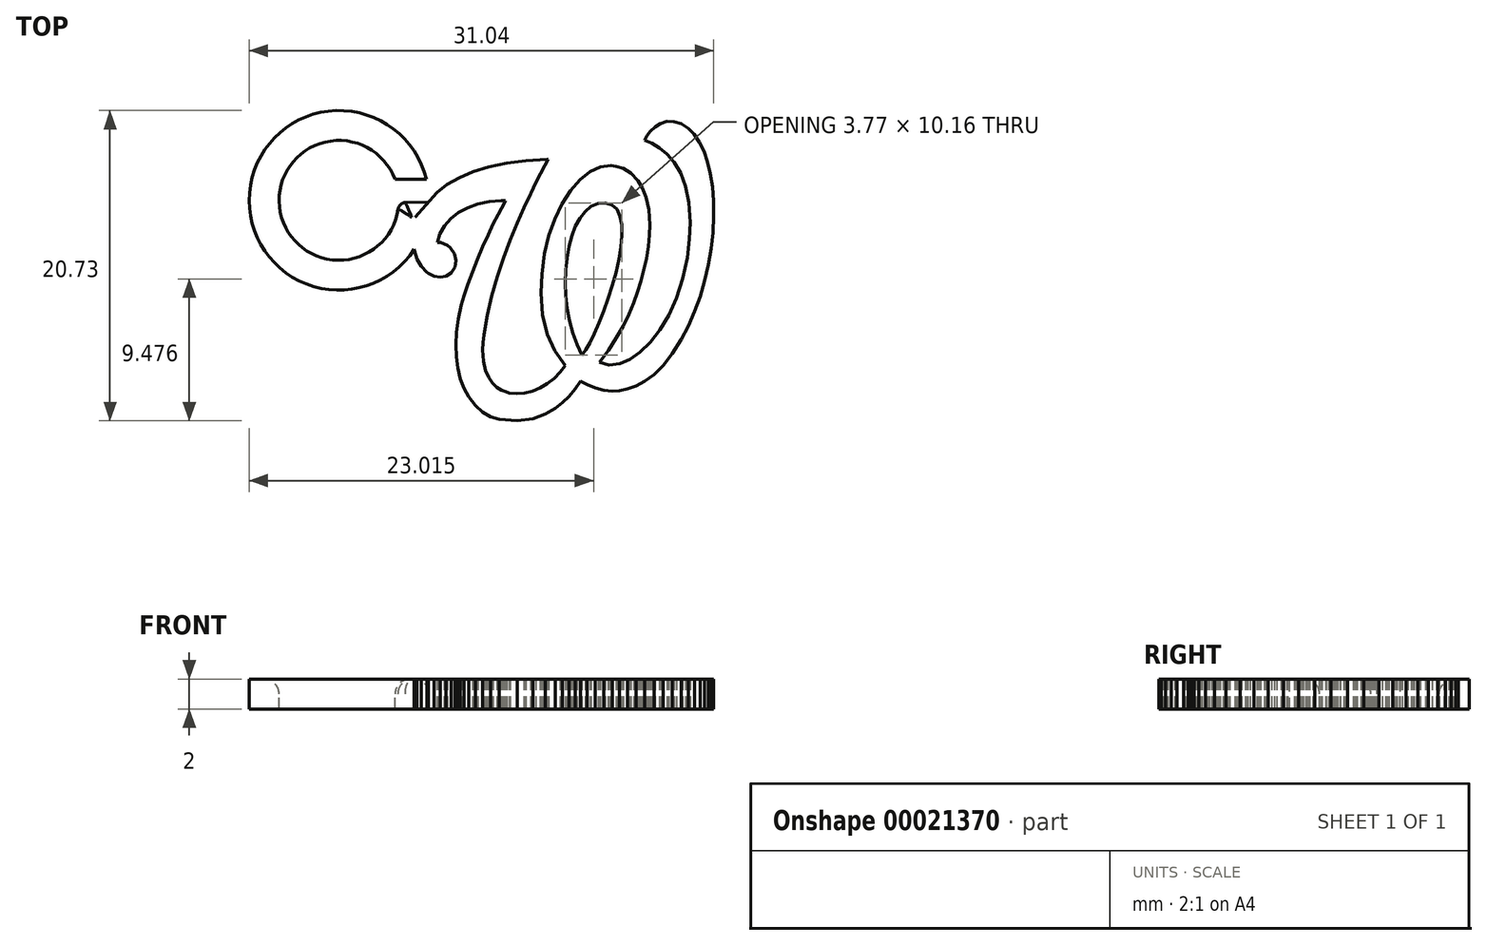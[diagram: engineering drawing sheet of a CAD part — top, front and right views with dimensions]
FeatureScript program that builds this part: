
annotation { "Feature Type Name" : "Feature", "Feature Type Description" : "" }
export const myFeature = defineFeature(function(context is Context, id is Id, definition is map)
    precondition{}
    {
        {
            var Q0;
            Q0=qCreatedBy(makeId("Top.planeOp"),FACE);
            var sketch = newSketch(context, id + "F0", { "sketchPlane" : qUnion([Q0])});
            skLineSegment(sketch, "E0", {"start": v(8.32, 9.54) * mm, "end": v(7.85, 9.84) * mm});
            skLineSegment(sketch, "E1", {"start": v(7.85, 9.84) * mm, "end": v(7.38, 10) * mm});
            skLineSegment(sketch, "E2", {"start": v(7.38, 10) * mm, "end": v(6.9, 10) * mm});
            skLineSegment(sketch, "E3", {"start": v(6.9, 10) * mm, "end": v(6.45, 9.86) * mm});
            skLineSegment(sketch, "E4", {"start": v(6.45, 9.86) * mm, "end": v(6.1, 9.64) * mm});
            skLineSegment(sketch, "E5", {"start": v(6.1, 9.64) * mm, "end": v(5.8, 9.36) * mm});
            skLineSegment(sketch, "E6", {"start": v(5.8, 9.36) * mm, "end": v(5.58, 9.04) * mm});
            skLineSegment(sketch, "E7", {"start": v(5.58, 9.04) * mm, "end": v(5.43, 8.73) * mm});
            skLineSegment(sketch, "E8", {"start": v(5.43, 8.73) * mm, "end": v(5.9, 8.53) * mm});
            skLineSegment(sketch, "E9", {"start": v(5.9, 8.53) * mm, "end": v(6.4, 8.24) * mm});
            skLineSegment(sketch, "E10", {"start": v(6.4, 8.24) * mm, "end": v(6.92, 7.83) * mm});
            skLineSegment(sketch, "E11", {"start": v(6.92, 7.83) * mm, "end": v(7.4, 7.27) * mm});
            skLineSegment(sketch, "E12", {"start": v(7.4, 7.27) * mm, "end": v(7.82, 6.56) * mm});
            skLineSegment(sketch, "E13", {"start": v(7.82, 6.56) * mm, "end": v(8.15, 5.66) * mm});
            skLineSegment(sketch, "E14", {"start": v(8.15, 5.66) * mm, "end": v(8.38, 4.56) * mm});
            skLineSegment(sketch, "E15", {"start": v(8.38, 4.56) * mm, "end": v(8.46, 3.25) * mm});
            skLineSegment(sketch, "E16", {"start": v(8.46, 3.25) * mm, "end": v(8.41, 2.13) * mm});
            skLineSegment(sketch, "E17", {"start": v(8.41, 2.13) * mm, "end": v(8.26, 0.9) * mm});
            skLineSegment(sketch, "E18", {"start": v(8.26, 0.9) * mm, "end": v(7.97, -0.51) * mm});
            skLineSegment(sketch, "E19", {"start": v(7.97, -0.51) * mm, "end": v(7.55, -1.8) * mm});
            skLineSegment(sketch, "E20", {"start": v(7.55, -1.8) * mm, "end": v(7.03, -2.93) * mm});
            skLineSegment(sketch, "E21", {"start": v(7.03, -2.93) * mm, "end": v(6.43, -3.92) * mm});
            skLineSegment(sketch, "E22", {"start": v(6.43, -3.92) * mm, "end": v(5.78, -4.75) * mm});
            skLineSegment(sketch, "E23", {"start": v(5.78, -4.75) * mm, "end": v(5.1, -5.41) * mm});
            skLineSegment(sketch, "E24", {"start": v(5.1, -5.41) * mm, "end": v(4.42, -5.9) * mm});
            skLineSegment(sketch, "E25", {"start": v(4.42, -5.9) * mm, "end": v(3.75, -6.18) * mm});
            skLineSegment(sketch, "E26", {"start": v(3.75, -6.18) * mm, "end": v(3.02, -6.27) * mm});
            skLineSegment(sketch, "E27", {"start": v(3.02, -6.27) * mm, "end": v(2.39, -6.08) * mm});
            skLineSegment(sketch, "E28", {"start": v(2.39, -6.08) * mm, "end": v(3, -5.28) * mm});
            skLineSegment(sketch, "E29", {"start": v(3, -5.28) * mm, "end": v(3.52, -4.47) * mm});
            skLineSegment(sketch, "E30", {"start": v(3.52, -4.47) * mm, "end": v(3.97, -3.67) * mm});
            skLineSegment(sketch, "E31", {"start": v(3.97, -3.67) * mm, "end": v(4.36, -2.88) * mm});
            skLineSegment(sketch, "E32", {"start": v(4.36, -2.88) * mm, "end": v(4.68, -2.12) * mm});
            skLineSegment(sketch, "E33", {"start": v(4.68, -2.12) * mm, "end": v(4.95, -1.39) * mm});
            skLineSegment(sketch, "E34", {"start": v(4.95, -1.39) * mm, "end": v(5.16, -0.7) * mm});
            skLineSegment(sketch, "E35", {"start": v(5.16, -0.7) * mm, "end": v(5.33, -0.06) * mm});
            skLineSegment(sketch, "E36", {"start": v(5.33, -0.06) * mm, "end": v(5.53, 0.84) * mm});
            skLineSegment(sketch, "E37", {"start": v(5.53, 0.84) * mm, "end": v(5.66, 1.67) * mm});
            skLineSegment(sketch, "E38", {"start": v(5.66, 1.67) * mm, "end": v(5.74, 2.4) * mm});
            skLineSegment(sketch, "E39", {"start": v(5.74, 2.4) * mm, "end": v(5.76, 3.08) * mm});
            skLineSegment(sketch, "E40", {"start": v(5.76, 3.08) * mm, "end": v(5.7, 4.1) * mm});
            skLineSegment(sketch, "E41", {"start": v(5.7, 4.1) * mm, "end": v(5.52, 4.93) * mm});
            skLineSegment(sketch, "E42", {"start": v(5.52, 4.93) * mm, "end": v(5.26, 5.57) * mm});
            skLineSegment(sketch, "E43", {"start": v(5.26, 5.57) * mm, "end": v(4.97, 6.05) * mm});
            skLineSegment(sketch, "E44", {"start": v(4.97, 6.05) * mm, "end": v(4.48, 6.56) * mm});
            skLineSegment(sketch, "E45", {"start": v(4.48, 6.56) * mm, "end": v(3.98, 6.86) * mm});
            skLineSegment(sketch, "E46", {"start": v(3.98, 6.86) * mm, "end": v(3.52, 7) * mm});
            skLineSegment(sketch, "E47", {"start": v(3.52, 7) * mm, "end": v(3.15, 7.06) * mm});
            skLineSegment(sketch, "E48", {"start": v(3.15, 7.06) * mm, "end": v(2.46, 6.96) * mm});
            skLineSegment(sketch, "E49", {"start": v(2.46, 6.96) * mm, "end": v(1.77, 6.64) * mm});
            skLineSegment(sketch, "E50", {"start": v(1.77, 6.64) * mm, "end": v(1.1, 6.1) * mm});
            skLineSegment(sketch, "E51", {"start": v(1.1, 6.1) * mm, "end": v(0.47, 5.37) * mm});
            skLineSegment(sketch, "E52", {"start": v(0.47, 5.37) * mm, "end": v(-0.1, 4.5) * mm});
            skLineSegment(sketch, "E53", {"start": v(-0.1, 4.5) * mm, "end": v(-0.6, 3.48) * mm});
            skLineSegment(sketch, "E54", {"start": v(-0.6, 3.48) * mm, "end": v(-1, 2.36) * mm});
            skLineSegment(sketch, "E55", {"start": v(-1, 2.36) * mm, "end": v(-1.27, 1.16) * mm});
            skLineSegment(sketch, "E56", {"start": v(-1.27, 1.16) * mm, "end": v(-1.46, -0.2) * mm});
            skLineSegment(sketch, "E57", {"start": v(-1.46, -0.2) * mm, "end": v(-1.52, -1.46) * mm});
            skLineSegment(sketch, "E58", {"start": v(-1.52, -1.46) * mm, "end": v(-1.42, -2.92) * mm});
            skLineSegment(sketch, "E59", {"start": v(-1.42, -2.92) * mm, "end": v(-1.11, -4.21) * mm});
            skLineSegment(sketch, "E60", {"start": v(-1.11, -4.21) * mm, "end": v(-0.6, -5.34) * mm});
            skLineSegment(sketch, "E61", {"start": v(-0.6, -5.34) * mm, "end": v(0.11, -6.3) * mm});
            skLineSegment(sketch, "E62", {"start": v(0.11, -6.3) * mm, "end": v(-0.23, -6.76) * mm});
            skLineSegment(sketch, "E63", {"start": v(-0.23, -6.76) * mm, "end": v(-0.63, -7.17) * mm});
            skLineSegment(sketch, "E64", {"start": v(-0.63, -7.17) * mm, "end": v(-1.08, -7.52) * mm});
            skLineSegment(sketch, "E65", {"start": v(-1.08, -7.52) * mm, "end": v(-1.57, -7.8) * mm});
            skLineSegment(sketch, "E66", {"start": v(-1.57, -7.8) * mm, "end": v(-2.09, -8.02) * mm});
            skLineSegment(sketch, "E67", {"start": v(-2.09, -8.02) * mm, "end": v(-2.61, -8.16) * mm});
            skLineSegment(sketch, "E68", {"start": v(-2.61, -8.16) * mm, "end": v(-3.13, -8.2) * mm});
            skLineSegment(sketch, "E69", {"start": v(-3.13, -8.2) * mm, "end": v(-3.63, -8.14) * mm});
            skLineSegment(sketch, "E70", {"start": v(-3.63, -8.14) * mm, "end": v(-3.87, -8.07) * mm});
            skLineSegment(sketch, "E71", {"start": v(-3.87, -8.07) * mm, "end": v(-4.15, -7.95) * mm});
            skLineSegment(sketch, "E72", {"start": v(-4.15, -7.95) * mm, "end": v(-4.45, -7.76) * mm});
            skLineSegment(sketch, "E73", {"start": v(-4.45, -7.76) * mm, "end": v(-4.74, -7.48) * mm});
            skLineSegment(sketch, "E74", {"start": v(-4.74, -7.48) * mm, "end": v(-5, -7.11) * mm});
            skLineSegment(sketch, "E75", {"start": v(-5, -7.11) * mm, "end": v(-5.21, -6.63) * mm});
            skLineSegment(sketch, "E76", {"start": v(-5.21, -6.63) * mm, "end": v(-5.36, -6.02) * mm});
            skLineSegment(sketch, "E77", {"start": v(-5.36, -6.02) * mm, "end": v(-5.4, -5.27) * mm});
            skLineSegment(sketch, "E78", {"start": v(-5.4, -5.27) * mm, "end": v(-5.39, -4.78) * mm});
            skLineSegment(sketch, "E79", {"start": v(-5.39, -4.78) * mm, "end": v(-5.33, -4.23) * mm});
            skLineSegment(sketch, "E80", {"start": v(-5.33, -4.23) * mm, "end": v(-5.1, -2.95) * mm});
            skLineSegment(sketch, "E81", {"start": v(-5.1, -2.95) * mm, "end": v(-4.8, -1.66) * mm});
            skLineSegment(sketch, "E82", {"start": v(-4.8, -1.66) * mm, "end": v(-4.43, -0.37) * mm});
            skLineSegment(sketch, "E83", {"start": v(-4.43, -0.37) * mm, "end": v(-4, 0.88) * mm});
            skLineSegment(sketch, "E84", {"start": v(-4, 0.88) * mm, "end": v(-3.56, 2.08) * mm});
            skLineSegment(sketch, "E85", {"start": v(-3.56, 2.08) * mm, "end": v(-3.1, 3.2) * mm});
            skLineSegment(sketch, "E86", {"start": v(-3.1, 3.2) * mm, "end": v(-2.64, 4.24) * mm});
            skLineSegment(sketch, "E87", {"start": v(-2.64, 4.24) * mm, "end": v(-2.21, 5.15) * mm});
            skLineSegment(sketch, "E88", {"start": v(-2.21, 5.15) * mm, "end": v(-2.19, 5.2) * mm});
            skLineSegment(sketch, "E89", {"start": v(-2.19, 5.2) * mm, "end": v(-1.84, 5.9) * mm});
            skLineSegment(sketch, "E90", {"start": v(-1.84, 5.9) * mm, "end": v(-1.53, 6.52) * mm});
            skLineSegment(sketch, "E91", {"start": v(-1.53, 6.52) * mm, "end": v(-1.26, 7.05) * mm});
            skLineSegment(sketch, "E92", {"start": v(-1.26, 7.05) * mm, "end": v(-1.03, 7.46) * mm});
            skLineSegment(sketch, "E93", {"start": v(-1.03, 7.46) * mm, "end": v(-1.1, 7.46) * mm});
            skLineSegment(sketch, "E94", {"start": v(-1.1, 7.46) * mm, "end": v(-2.51, 7.37) * mm});
            skLineSegment(sketch, "E95", {"start": v(-2.51, 7.37) * mm, "end": v(-3.81, 7.2) * mm});
            skLineSegment(sketch, "E96", {"start": v(-3.81, 7.2) * mm, "end": v(-4.99, 6.96) * mm});
            skLineSegment(sketch, "E97", {"start": v(-4.99, 6.96) * mm, "end": v(-6.05, 6.64) * mm});
            skLineSegment(sketch, "E98", {"start": v(-6.05, 6.64) * mm, "end": v(-6.98, 6.25) * mm});
            skLineSegment(sketch, "E99", {"start": v(-6.98, 6.25) * mm, "end": v(-7.79, 5.78) * mm});
            skLineSegment(sketch, "E100", {"start": v(-7.79, 5.78) * mm, "end": v(-8.47, 5.24) * mm});
            skLineSegment(sketch, "E101", {"start": v(-8.47, 5.24) * mm, "end": v(-9, 4.63) * mm});
            skLineSegment(sketch, "E102", {"start": v(-9, 4.63) * mm, "end": v(-9.05, 4.57) * mm});
            skLineSegment(sketch, "E103", {"start": v(-9.05, 4.57) * mm, "end": v(-9.17, 4.4) * mm});
            skLineSegment(sketch, "E104", {"start": v(-9.17, 4.4) * mm, "end": v(-9.34, 4.13) * mm});
            skLineSegment(sketch, "E105", {"start": v(-9.34, 4.13) * mm, "end": v(-9.53, 3.78) * mm});
            skLineSegment(sketch, "E106", {"start": v(-9.53, 3.78) * mm, "end": v(-9.72, 3.37) * mm});
            skLineSegment(sketch, "E107", {"start": v(-9.72, 3.37) * mm, "end": v(-9.88, 2.9) * mm});
            skLineSegment(sketch, "E108", {"start": v(-9.88, 2.9) * mm, "end": v(-10, 2.42) * mm});
            skLineSegment(sketch, "E109", {"start": v(-10, 2.42) * mm, "end": v(-10.03, 1.9) * mm});
            skLineSegment(sketch, "E110", {"start": v(-10.03, 1.9) * mm, "end": v(-9.96, 1.33) * mm});
            skLineSegment(sketch, "E111", {"start": v(-9.96, 1.33) * mm, "end": v(-9.8, 0.8) * mm});
            skLineSegment(sketch, "E112", {"start": v(-9.8, 0.8) * mm, "end": v(-9.51, 0.32) * mm});
            skLineSegment(sketch, "E113", {"start": v(-9.51, 0.32) * mm, "end": v(-9.12, -0.09) * mm});
            skLineSegment(sketch, "E114", {"start": v(-9.12, -0.09) * mm, "end": v(-9.04, -0.15) * mm});
            skLineSegment(sketch, "E115", {"start": v(-9.04, -0.15) * mm, "end": v(-8.65, -0.35) * mm});
            skLineSegment(sketch, "E116", {"start": v(-8.65, -0.35) * mm, "end": v(-8.24, -0.42) * mm});
            skLineSegment(sketch, "E117", {"start": v(-8.24, -0.42) * mm, "end": v(-7.85, -0.34) * mm});
            skLineSegment(sketch, "E118", {"start": v(-7.85, -0.34) * mm, "end": v(-7.5, -0.1) * mm});
            skLineSegment(sketch, "E119", {"start": v(-7.5, -0.1) * mm, "end": v(-7.26, 0.27) * mm});
            skLineSegment(sketch, "E120", {"start": v(-7.26, 0.27) * mm, "end": v(-7.2, 0.71) * mm});
            skLineSegment(sketch, "E121", {"start": v(-7.2, 0.71) * mm, "end": v(-7.3, 1.16) * mm});
            skLineSegment(sketch, "E122", {"start": v(-7.3, 1.16) * mm, "end": v(-7.56, 1.55) * mm});
            skLineSegment(sketch, "E123", {"start": v(-7.56, 1.55) * mm, "end": v(-7.76, 1.71) * mm});
            skLineSegment(sketch, "E124", {"start": v(-7.76, 1.71) * mm, "end": v(-7.97, 1.83) * mm});
            skLineSegment(sketch, "E125", {"start": v(-7.97, 1.83) * mm, "end": v(-8.2, 1.9) * mm});
            skLineSegment(sketch, "E126", {"start": v(-8.2, 1.9) * mm, "end": v(-8.43, 1.93) * mm});
            skLineSegment(sketch, "E127", {"start": v(-8.43, 1.93) * mm, "end": v(-8.44, 1.93) * mm});
            skLineSegment(sketch, "E128", {"start": v(-8.44, 1.93) * mm, "end": v(-8.27, 2.5) * mm});
            skLineSegment(sketch, "E129", {"start": v(-8.27, 2.5) * mm, "end": v(-7.96, 3.02) * mm});
            skLineSegment(sketch, "E130", {"start": v(-7.96, 3.02) * mm, "end": v(-7.54, 3.5) * mm});
            skLineSegment(sketch, "E131", {"start": v(-7.54, 3.5) * mm, "end": v(-7.02, 3.9) * mm});
            skLineSegment(sketch, "E132", {"start": v(-7.02, 3.9) * mm, "end": v(-6.4, 4.24) * mm});
            skLineSegment(sketch, "E133", {"start": v(-6.4, 4.24) * mm, "end": v(-5.72, 4.5) * mm});
            skLineSegment(sketch, "E134", {"start": v(-5.72, 4.5) * mm, "end": v(-4.97, 4.65) * mm});
            skLineSegment(sketch, "E135", {"start": v(-4.97, 4.65) * mm, "end": v(-4.17, 4.7) * mm});
            skLineSegment(sketch, "E136", {"start": v(-4.17, 4.7) * mm, "end": v(-3.88, 4.7) * mm});
            skLineSegment(sketch, "E137", {"start": v(-3.88, 4.7) * mm, "end": v(-3.92, 4.62) * mm});
            skLineSegment(sketch, "E138", {"start": v(-3.92, 4.62) * mm, "end": v(-4.38, 3.77) * mm});
            skLineSegment(sketch, "E139", {"start": v(-4.38, 3.77) * mm, "end": v(-4.7, 3.15) * mm});
            skLineSegment(sketch, "E140", {"start": v(-4.7, 3.15) * mm, "end": v(-5.05, 2.42) * mm});
            skLineSegment(sketch, "E141", {"start": v(-5.05, 2.42) * mm, "end": v(-5.4, 1.62) * mm});
            skLineSegment(sketch, "E142", {"start": v(-5.4, 1.62) * mm, "end": v(-5.76, 0.78) * mm});
            skLineSegment(sketch, "E143", {"start": v(-5.76, 0.78) * mm, "end": v(-6.1, -0.07) * mm});
            skLineSegment(sketch, "E144", {"start": v(-6.1, -0.07) * mm, "end": v(-6.4, -0.88) * mm});
            skLineSegment(sketch, "E145", {"start": v(-6.4, -0.88) * mm, "end": v(-6.65, -1.63) * mm});
            skLineSegment(sketch, "E146", {"start": v(-6.65, -1.63) * mm, "end": v(-6.83, -2.28) * mm});
            skLineSegment(sketch, "E147", {"start": v(-6.83, -2.28) * mm, "end": v(-7.03, -3.2) * mm});
            skLineSegment(sketch, "E148", {"start": v(-7.03, -3.2) * mm, "end": v(-7.15, -4.08) * mm});
            skLineSegment(sketch, "E149", {"start": v(-7.15, -4.08) * mm, "end": v(-7.2, -4.92) * mm});
            skLineSegment(sketch, "E150", {"start": v(-7.2, -4.92) * mm, "end": v(-7.17, -5.73) * mm});
            skLineSegment(sketch, "E151", {"start": v(-7.17, -5.73) * mm, "end": v(-7.07, -6.48) * mm});
            skLineSegment(sketch, "E152", {"start": v(-7.07, -6.48) * mm, "end": v(-6.9, -7.18) * mm});
            skLineSegment(sketch, "E153", {"start": v(-6.9, -7.18) * mm, "end": v(-6.65, -7.83) * mm});
            skLineSegment(sketch, "E154", {"start": v(-6.65, -7.83) * mm, "end": v(-6.33, -8.41) * mm});
            skLineSegment(sketch, "E155", {"start": v(-6.33, -8.41) * mm, "end": v(-5.9, -8.97) * mm});
            skLineSegment(sketch, "E156", {"start": v(-5.9, -8.97) * mm, "end": v(-5.41, -9.41) * mm});
            skLineSegment(sketch, "E157", {"start": v(-5.41, -9.41) * mm, "end": v(-4.87, -9.73) * mm});
            skLineSegment(sketch, "E158", {"start": v(-4.87, -9.73) * mm, "end": v(-4.3, -9.9) * mm});
            skLineSegment(sketch, "E159", {"start": v(-4.3, -9.9) * mm, "end": v(-3.09, -10) * mm});
            skLineSegment(sketch, "E160", {"start": v(-3.09, -10) * mm, "end": v(-2.06, -9.85) * mm});
            skLineSegment(sketch, "E161", {"start": v(-2.06, -9.85) * mm, "end": v(-1.2, -9.54) * mm});
            skLineSegment(sketch, "E162", {"start": v(-1.2, -9.54) * mm, "end": v(-0.55, -9.16) * mm});
            skLineSegment(sketch, "E163", {"start": v(-0.55, -9.16) * mm, "end": v(-0.08, -8.8) * mm});
            skLineSegment(sketch, "E164", {"start": v(-0.08, -8.8) * mm, "end": v(0.36, -8.36) * mm});
            skLineSegment(sketch, "E165", {"start": v(0.36, -8.36) * mm, "end": v(0.77, -7.87) * mm});
            skLineSegment(sketch, "E166", {"start": v(0.77, -7.87) * mm, "end": v(1.13, -7.34) * mm});
            skLineSegment(sketch, "E167", {"start": v(1.13, -7.34) * mm, "end": v(1.57, -7.6) * mm});
            skLineSegment(sketch, "E168", {"start": v(1.57, -7.6) * mm, "end": v(2.1, -7.81) * mm});
            skLineSegment(sketch, "E169", {"start": v(2.1, -7.81) * mm, "end": v(2.68, -7.97) * mm});
            skLineSegment(sketch, "E170", {"start": v(2.68, -7.97) * mm, "end": v(3.24, -8.02) * mm});
            skLineSegment(sketch, "E171", {"start": v(3.24, -8.02) * mm, "end": v(3.73, -7.99) * mm});
            skLineSegment(sketch, "E172", {"start": v(3.73, -7.99) * mm, "end": v(4.26, -7.87) * mm});
            skLineSegment(sketch, "E173", {"start": v(4.26, -7.87) * mm, "end": v(4.83, -7.67) * mm});
            skLineSegment(sketch, "E174", {"start": v(4.83, -7.67) * mm, "end": v(5.42, -7.35) * mm});
            skLineSegment(sketch, "E175", {"start": v(5.42, -7.35) * mm, "end": v(6.03, -6.9) * mm});
            skLineSegment(sketch, "E176", {"start": v(6.03, -6.9) * mm, "end": v(6.65, -6.3) * mm});
            skLineSegment(sketch, "E177", {"start": v(6.65, -6.3) * mm, "end": v(7.26, -5.53) * mm});
            skLineSegment(sketch, "E178", {"start": v(7.26, -5.53) * mm, "end": v(7.86, -4.58) * mm});
            skLineSegment(sketch, "E179", {"start": v(7.86, -4.58) * mm, "end": v(8.33, -3.67) * mm});
            skLineSegment(sketch, "E180", {"start": v(8.33, -3.67) * mm, "end": v(8.75, -2.7) * mm});
            skLineSegment(sketch, "E181", {"start": v(8.75, -2.7) * mm, "end": v(9.11, -1.7) * mm});
            skLineSegment(sketch, "E182", {"start": v(9.11, -1.7) * mm, "end": v(9.42, -0.66) * mm});
            skLineSegment(sketch, "E183", {"start": v(9.42, -0.66) * mm, "end": v(9.67, 0.41) * mm});
            skLineSegment(sketch, "E184", {"start": v(9.67, 0.41) * mm, "end": v(9.85, 1.5) * mm});
            skLineSegment(sketch, "E185", {"start": v(9.85, 1.5) * mm, "end": v(9.97, 2.59) * mm});
            skLineSegment(sketch, "E186", {"start": v(9.97, 2.59) * mm, "end": v(10.03, 3.68) * mm});
            skLineSegment(sketch, "E187", {"start": v(10.03, 3.68) * mm, "end": v(10.02, 4.69) * mm});
            skLineSegment(sketch, "E188", {"start": v(10.02, 4.69) * mm, "end": v(9.94, 5.63) * mm});
            skLineSegment(sketch, "E189", {"start": v(9.94, 5.63) * mm, "end": v(9.8, 6.5) * mm});
            skLineSegment(sketch, "E190", {"start": v(9.8, 6.5) * mm, "end": v(9.62, 7.3) * mm});
            skLineSegment(sketch, "E191", {"start": v(9.62, 7.3) * mm, "end": v(9.37, 8.01) * mm});
            skLineSegment(sketch, "E192", {"start": v(9.37, 8.01) * mm, "end": v(9.07, 8.63) * mm});
            skLineSegment(sketch, "E193", {"start": v(9.07, 8.63) * mm, "end": v(8.72, 9.14) * mm});
            skLineSegment(sketch, "E194", {"start": v(8.72, 9.14) * mm, "end": v(8.32, 9.54) * mm});
            skLineSegment(sketch, "E195", {"start": v(2.79, 4.56) * mm, "end": v(3.24, 4.43) * mm});
            skLineSegment(sketch, "E196", {"start": v(3.24, 4.43) * mm, "end": v(3.56, 4.13) * mm});
            skLineSegment(sketch, "E197", {"start": v(3.56, 4.13) * mm, "end": v(3.77, 3.67) * mm});
            skLineSegment(sketch, "E198", {"start": v(3.77, 3.67) * mm, "end": v(3.88, 3.1) * mm});
            skLineSegment(sketch, "E199", {"start": v(3.88, 3.1) * mm, "end": v(3.89, 2.4) * mm});
            skLineSegment(sketch, "E200", {"start": v(3.89, 2.4) * mm, "end": v(3.82, 1.63) * mm});
            skLineSegment(sketch, "E201", {"start": v(3.82, 1.63) * mm, "end": v(3.69, 0.8) * mm});
            skLineSegment(sketch, "E202", {"start": v(3.69, 0.8) * mm, "end": v(3.5, -0.07) * mm});
            skLineSegment(sketch, "E203", {"start": v(3.5, -0.07) * mm, "end": v(3.25, -0.95) * mm});
            skLineSegment(sketch, "E204", {"start": v(3.25, -0.95) * mm, "end": v(2.98, -1.83) * mm});
            skLineSegment(sketch, "E205", {"start": v(2.98, -1.83) * mm, "end": v(2.68, -2.67) * mm});
            skLineSegment(sketch, "E206", {"start": v(2.68, -2.67) * mm, "end": v(2.37, -3.46) * mm});
            skLineSegment(sketch, "E207", {"start": v(2.37, -3.46) * mm, "end": v(2.06, -4.17) * mm});
            skLineSegment(sketch, "E208", {"start": v(2.06, -4.17) * mm, "end": v(1.76, -4.78) * mm});
            skLineSegment(sketch, "E209", {"start": v(1.76, -4.78) * mm, "end": v(1.48, -5.26) * mm});
            skLineSegment(sketch, "E210", {"start": v(1.48, -5.26) * mm, "end": v(1.23, -5.6) * mm});
            skLineSegment(sketch, "E211", {"start": v(1.23, -5.6) * mm, "end": v(0.9, -4.9) * mm});
            skLineSegment(sketch, "E212", {"start": v(0.9, -4.9) * mm, "end": v(0.62, -4.14) * mm});
            skLineSegment(sketch, "E213", {"start": v(0.62, -4.14) * mm, "end": v(0.4, -3.33) * mm});
            skLineSegment(sketch, "E214", {"start": v(0.4, -3.33) * mm, "end": v(0.25, -2.49) * mm});
            skLineSegment(sketch, "E215", {"start": v(0.25, -2.49) * mm, "end": v(0.16, -1.63) * mm});
            skLineSegment(sketch, "E216", {"start": v(0.16, -1.63) * mm, "end": v(0.12, -0.78) * mm});
            skLineSegment(sketch, "E217", {"start": v(0.12, -0.78) * mm, "end": v(0.14, 0.07) * mm});
            skLineSegment(sketch, "E218", {"start": v(0.14, 0.07) * mm, "end": v(0.22, 0.88) * mm});
            skLineSegment(sketch, "E219", {"start": v(0.22, 0.88) * mm, "end": v(0.36, 1.65) * mm});
            skLineSegment(sketch, "E220", {"start": v(0.36, 1.65) * mm, "end": v(0.55, 2.36) * mm});
            skLineSegment(sketch, "E221", {"start": v(0.55, 2.36) * mm, "end": v(0.8, 3) * mm});
            skLineSegment(sketch, "E222", {"start": v(0.8, 3) * mm, "end": v(1.09, 3.55) * mm});
            skLineSegment(sketch, "E223", {"start": v(1.09, 3.55) * mm, "end": v(1.44, 4) * mm});
            skLineSegment(sketch, "E224", {"start": v(1.44, 4) * mm, "end": v(1.84, 4.32) * mm});
            skLineSegment(sketch, "E225", {"start": v(1.84, 4.32) * mm, "end": v(2.29, 4.51) * mm});
            skLineSegment(sketch, "E226", {"start": v(2.29, 4.51) * mm, "end": v(2.79, 4.56) * mm});
            skSolve(sketch);
        }
        {
            var Q0;
            Q0 = qSketchRegion(id + "F0", true);
            extrude(context, id + "F1", {"entities" : qUnion([Q0]), "depth" : 2 * mm});
        }
        {
            var Q0;
            Q0=makeQuery(id+"F1.opExtrude","CAP_FACE",FACE,{"disambiguationData":[OSD([sQuery(id+"F0.wireOp",EDGE,"E0"),sQuery(id+"F0.wireOp",EDGE,"E1"),sQuery(id+"F0.wireOp",EDGE,"E2"),sQuery(id+"F0.wireOp",EDGE,"E3"),sQuery(id+"F0.wireOp",EDGE,"E4"),sQuery(id+"F0.wireOp",EDGE,"E5"),sQuery(id+"F0.wireOp",EDGE,"E6"),sQuery(id+"F0.wireOp",EDGE,"E7"),sQuery(id+"F0.wireOp",EDGE,"E8"),sQuery(id+"F0.wireOp",EDGE,"E9"),sQuery(id+"F0.wireOp",EDGE,"E10"),sQuery(id+"F0.wireOp",EDGE,"E11"),sQuery(id+"F0.wireOp",EDGE,"E12"),sQuery(id+"F0.wireOp",EDGE,"E13"),sQuery(id+"F0.wireOp",EDGE,"E14"),sQuery(id+"F0.wireOp",EDGE,"E15"),sQuery(id+"F0.wireOp",EDGE,"E16"),sQuery(id+"F0.wireOp",EDGE,"E17"),sQuery(id+"F0.wireOp",EDGE,"E18"),sQuery(id+"F0.wireOp",EDGE,"E19"),sQuery(id+"F0.wireOp",EDGE,"E20"),sQuery(id+"F0.wireOp",EDGE,"E21"),sQuery(id+"F0.wireOp",EDGE,"E22"),sQuery(id+"F0.wireOp",EDGE,"E23"),sQuery(id+"F0.wireOp",EDGE,"E24"),sQuery(id+"F0.wireOp",EDGE,"E25"),sQuery(id+"F0.wireOp",EDGE,"E26"),sQuery(id+"F0.wireOp",EDGE,"E27"),sQuery(id+"F0.wireOp",EDGE,"E28"),sQuery(id+"F0.wireOp",EDGE,"E29"),sQuery(id+"F0.wireOp",EDGE,"E30"),sQuery(id+"F0.wireOp",EDGE,"E31"),sQuery(id+"F0.wireOp",EDGE,"E32"),sQuery(id+"F0.wireOp",EDGE,"E33"),sQuery(id+"F0.wireOp",EDGE,"E34"),sQuery(id+"F0.wireOp",EDGE,"E35"),sQuery(id+"F0.wireOp",EDGE,"E36"),sQuery(id+"F0.wireOp",EDGE,"E37"),sQuery(id+"F0.wireOp",EDGE,"E38"),sQuery(id+"F0.wireOp",EDGE,"E39"),sQuery(id+"F0.wireOp",EDGE,"E40"),sQuery(id+"F0.wireOp",EDGE,"E41"),sQuery(id+"F0.wireOp",EDGE,"E42"),sQuery(id+"F0.wireOp",EDGE,"E43"),sQuery(id+"F0.wireOp",EDGE,"E44"),sQuery(id+"F0.wireOp",EDGE,"E45"),sQuery(id+"F0.wireOp",EDGE,"E46"),sQuery(id+"F0.wireOp",EDGE,"E47"),sQuery(id+"F0.wireOp",EDGE,"E48"),sQuery(id+"F0.wireOp",EDGE,"E49"),sQuery(id+"F0.wireOp",EDGE,"E50"),sQuery(id+"F0.wireOp",EDGE,"E51"),sQuery(id+"F0.wireOp",EDGE,"E52"),sQuery(id+"F0.wireOp",EDGE,"E53"),sQuery(id+"F0.wireOp",EDGE,"E54"),sQuery(id+"F0.wireOp",EDGE,"E55"),sQuery(id+"F0.wireOp",EDGE,"E56"),sQuery(id+"F0.wireOp",EDGE,"E57"),sQuery(id+"F0.wireOp",EDGE,"E58"),sQuery(id+"F0.wireOp",EDGE,"E59"),sQuery(id+"F0.wireOp",EDGE,"E60"),sQuery(id+"F0.wireOp",EDGE,"E61"),sQuery(id+"F0.wireOp",EDGE,"E62"),sQuery(id+"F0.wireOp",EDGE,"E63"),sQuery(id+"F0.wireOp",EDGE,"E64"),sQuery(id+"F0.wireOp",EDGE,"E65"),sQuery(id+"F0.wireOp",EDGE,"E66"),sQuery(id+"F0.wireOp",EDGE,"E67"),sQuery(id+"F0.wireOp",EDGE,"E68"),sQuery(id+"F0.wireOp",EDGE,"E69"),sQuery(id+"F0.wireOp",EDGE,"E70"),sQuery(id+"F0.wireOp",EDGE,"E71"),sQuery(id+"F0.wireOp",EDGE,"E72"),sQuery(id+"F0.wireOp",EDGE,"E73"),sQuery(id+"F0.wireOp",EDGE,"E74"),sQuery(id+"F0.wireOp",EDGE,"E75"),sQuery(id+"F0.wireOp",EDGE,"E76"),sQuery(id+"F0.wireOp",EDGE,"E77"),sQuery(id+"F0.wireOp",EDGE,"E78"),sQuery(id+"F0.wireOp",EDGE,"E79"),sQuery(id+"F0.wireOp",EDGE,"E80"),sQuery(id+"F0.wireOp",EDGE,"E81"),sQuery(id+"F0.wireOp",EDGE,"E82"),sQuery(id+"F0.wireOp",EDGE,"E83"),sQuery(id+"F0.wireOp",EDGE,"E84"),sQuery(id+"F0.wireOp",EDGE,"E85"),sQuery(id+"F0.wireOp",EDGE,"E86"),sQuery(id+"F0.wireOp",EDGE,"E87"),sQuery(id+"F0.wireOp",EDGE,"E88"),sQuery(id+"F0.wireOp",EDGE,"E89"),sQuery(id+"F0.wireOp",EDGE,"E90"),sQuery(id+"F0.wireOp",EDGE,"E91"),sQuery(id+"F0.wireOp",EDGE,"E92"),sQuery(id+"F0.wireOp",EDGE,"E93"),sQuery(id+"F0.wireOp",EDGE,"E94"),sQuery(id+"F0.wireOp",EDGE,"E95"),sQuery(id+"F0.wireOp",EDGE,"E96"),sQuery(id+"F0.wireOp",EDGE,"E97"),sQuery(id+"F0.wireOp",EDGE,"E98"),sQuery(id+"F0.wireOp",EDGE,"E99"),sQuery(id+"F0.wireOp",EDGE,"E100"),sQuery(id+"F0.wireOp",EDGE,"E101"),sQuery(id+"F0.wireOp",EDGE,"E102"),sQuery(id+"F0.wireOp",EDGE,"E103"),sQuery(id+"F0.wireOp",EDGE,"E104"),sQuery(id+"F0.wireOp",EDGE,"E105"),sQuery(id+"F0.wireOp",EDGE,"E106"),sQuery(id+"F0.wireOp",EDGE,"E107"),sQuery(id+"F0.wireOp",EDGE,"E108"),sQuery(id+"F0.wireOp",EDGE,"E109"),sQuery(id+"F0.wireOp",EDGE,"E110"),sQuery(id+"F0.wireOp",EDGE,"E111"),sQuery(id+"F0.wireOp",EDGE,"E112"),sQuery(id+"F0.wireOp",EDGE,"E113"),sQuery(id+"F0.wireOp",EDGE,"E114"),sQuery(id+"F0.wireOp",EDGE,"E115"),sQuery(id+"F0.wireOp",EDGE,"E116"),sQuery(id+"F0.wireOp",EDGE,"E117"),sQuery(id+"F0.wireOp",EDGE,"E118"),sQuery(id+"F0.wireOp",EDGE,"E119"),sQuery(id+"F0.wireOp",EDGE,"E120"),sQuery(id+"F0.wireOp",EDGE,"E121"),sQuery(id+"F0.wireOp",EDGE,"E122"),sQuery(id+"F0.wireOp",EDGE,"E123"),sQuery(id+"F0.wireOp",EDGE,"E124"),sQuery(id+"F0.wireOp",EDGE,"E125"),sQuery(id+"F0.wireOp",EDGE,"E126"),sQuery(id+"F0.wireOp",EDGE,"E127"),sQuery(id+"F0.wireOp",EDGE,"E128"),sQuery(id+"F0.wireOp",EDGE,"E129"),sQuery(id+"F0.wireOp",EDGE,"E130"),sQuery(id+"F0.wireOp",EDGE,"E131"),sQuery(id+"F0.wireOp",EDGE,"E132"),sQuery(id+"F0.wireOp",EDGE,"E133"),sQuery(id+"F0.wireOp",EDGE,"E134"),sQuery(id+"F0.wireOp",EDGE,"E135"),sQuery(id+"F0.wireOp",EDGE,"E136"),sQuery(id+"F0.wireOp",EDGE,"E137"),sQuery(id+"F0.wireOp",EDGE,"E138"),sQuery(id+"F0.wireOp",EDGE,"E139"),sQuery(id+"F0.wireOp",EDGE,"E140"),sQuery(id+"F0.wireOp",EDGE,"E141"),sQuery(id+"F0.wireOp",EDGE,"E142"),sQuery(id+"F0.wireOp",EDGE,"E143"),sQuery(id+"F0.wireOp",EDGE,"E144"),sQuery(id+"F0.wireOp",EDGE,"E145"),sQuery(id+"F0.wireOp",EDGE,"E146"),sQuery(id+"F0.wireOp",EDGE,"E147"),sQuery(id+"F0.wireOp",EDGE,"E148"),sQuery(id+"F0.wireOp",EDGE,"E149"),sQuery(id+"F0.wireOp",EDGE,"E150"),sQuery(id+"F0.wireOp",EDGE,"E151"),sQuery(id+"F0.wireOp",EDGE,"E152"),sQuery(id+"F0.wireOp",EDGE,"E153"),sQuery(id+"F0.wireOp",EDGE,"E154"),sQuery(id+"F0.wireOp",EDGE,"E155"),sQuery(id+"F0.wireOp",EDGE,"E156"),sQuery(id+"F0.wireOp",EDGE,"E157"),sQuery(id+"F0.wireOp",EDGE,"E158"),sQuery(id+"F0.wireOp",EDGE,"E159"),sQuery(id+"F0.wireOp",EDGE,"E160"),sQuery(id+"F0.wireOp",EDGE,"E161"),sQuery(id+"F0.wireOp",EDGE,"E162"),sQuery(id+"F0.wireOp",EDGE,"E163"),sQuery(id+"F0.wireOp",EDGE,"E164"),sQuery(id+"F0.wireOp",EDGE,"E165"),sQuery(id+"F0.wireOp",EDGE,"E166"),sQuery(id+"F0.wireOp",EDGE,"E167"),sQuery(id+"F0.wireOp",EDGE,"E168"),sQuery(id+"F0.wireOp",EDGE,"E169"),sQuery(id+"F0.wireOp",EDGE,"E170"),sQuery(id+"F0.wireOp",EDGE,"E171"),sQuery(id+"F0.wireOp",EDGE,"E172"),sQuery(id+"F0.wireOp",EDGE,"E173"),sQuery(id+"F0.wireOp",EDGE,"E174"),sQuery(id+"F0.wireOp",EDGE,"E175"),sQuery(id+"F0.wireOp",EDGE,"E176"),sQuery(id+"F0.wireOp",EDGE,"E177"),sQuery(id+"F0.wireOp",EDGE,"E178"),sQuery(id+"F0.wireOp",EDGE,"E179"),sQuery(id+"F0.wireOp",EDGE,"E180"),sQuery(id+"F0.wireOp",EDGE,"E181"),sQuery(id+"F0.wireOp",EDGE,"E182"),sQuery(id+"F0.wireOp",EDGE,"E183"),sQuery(id+"F0.wireOp",EDGE,"E184"),sQuery(id+"F0.wireOp",EDGE,"E185"),sQuery(id+"F0.wireOp",EDGE,"E186"),sQuery(id+"F0.wireOp",EDGE,"E187"),sQuery(id+"F0.wireOp",EDGE,"E188"),sQuery(id+"F0.wireOp",EDGE,"E189"),sQuery(id+"F0.wireOp",EDGE,"E190"),sQuery(id+"F0.wireOp",EDGE,"E191"),sQuery(id+"F0.wireOp",EDGE,"E192"),sQuery(id+"F0.wireOp",EDGE,"E193"),sQuery(id+"F0.wireOp",EDGE,"E194"),sQuery(id+"F0.wireOp",EDGE,"E195"),sQuery(id+"F0.wireOp",EDGE,"E196"),sQuery(id+"F0.wireOp",EDGE,"E197"),sQuery(id+"F0.wireOp",EDGE,"E198"),sQuery(id+"F0.wireOp",EDGE,"E199"),sQuery(id+"F0.wireOp",EDGE,"E200"),sQuery(id+"F0.wireOp",EDGE,"E201"),sQuery(id+"F0.wireOp",EDGE,"E202"),sQuery(id+"F0.wireOp",EDGE,"E203"),sQuery(id+"F0.wireOp",EDGE,"E204"),sQuery(id+"F0.wireOp",EDGE,"E205"),sQuery(id+"F0.wireOp",EDGE,"E206"),sQuery(id+"F0.wireOp",EDGE,"E207"),sQuery(id+"F0.wireOp",EDGE,"E208"),sQuery(id+"F0.wireOp",EDGE,"E209"),sQuery(id+"F0.wireOp",EDGE,"E210"),sQuery(id+"F0.wireOp",EDGE,"E211"),sQuery(id+"F0.wireOp",EDGE,"E212"),sQuery(id+"F0.wireOp",EDGE,"E213"),sQuery(id+"F0.wireOp",EDGE,"E214"),sQuery(id+"F0.wireOp",EDGE,"E215"),sQuery(id+"F0.wireOp",EDGE,"E216"),sQuery(id+"F0.wireOp",EDGE,"E217"),sQuery(id+"F0.wireOp",EDGE,"E218"),sQuery(id+"F0.wireOp",EDGE,"E219"),sQuery(id+"F0.wireOp",EDGE,"E220"),sQuery(id+"F0.wireOp",EDGE,"E221"),sQuery(id+"F0.wireOp",EDGE,"E222"),sQuery(id+"F0.wireOp",EDGE,"E223"),sQuery(id+"F0.wireOp",EDGE,"E224"),sQuery(id+"F0.wireOp",EDGE,"E225"),sQuery(id+"F0.wireOp",EDGE,"E226")])],"isStart":false});
            var sketch = newSketch(context, id + "F2", { "sketchPlane" : qUnion([Q0])});
            skArc(sketch, "E227", {"start": v(-9.17, 6.13) * mm, "mid": v(-20.97, 4.07) * mm, "end": v(-9, 4.63) * mm});
            skLineSegment(sketch, "E228", {"start": v(-9, 4.63) * mm, "end": v(-10.57, 4.58) * mm});
            skLineSegment(sketch, "E229", {"start": v(-9.17, 6.13) * mm, "end": v(-11.26, 6.13) * mm});
            skArc(sketch, "E230", {"start": v(-11.26, 6.13) * mm, "mid": v(-18.98, 4.3) * mm, "end": v(-11.05, 4.15) * mm});
            skPoint(sketch, "E231.visualSharp", {"position": v(-11.01, 4.57) * mm});
            skArc(sketch, "E231.filletArc", {"start": v(-10.57, 4.58) * mm, "mid": v(-10.89, 4.45) * mm, "end": v(-11.05, 4.15) * mm});
            skSolve(sketch);
        }
        {
            var Q0;
            Q0 = qSketchRegion(id + "F2", true);
            extrude(context, id + "F3", {"entities" : qUnion([Q0]), "operationType" : NewBodyOperationType.ADD, "oppositeDirection" : true, "depth" : 2 * mm});
        }
        {
            var Q0;
            Q0=makeQuery(id+"F3.opExtrude","CAP_EDGE",EDGE,{"disambiguationData":[OSD([sQuery(id+"F2.wireOp",EDGE,"E230")])],"isStart":true});
            fillet(context, id + "F4", {"entities" : qUnion([Q0]), "radius" : 1 * mm, "tangentPropagation" : true, "allowEdgeOverflow" : false});
        }
    });
